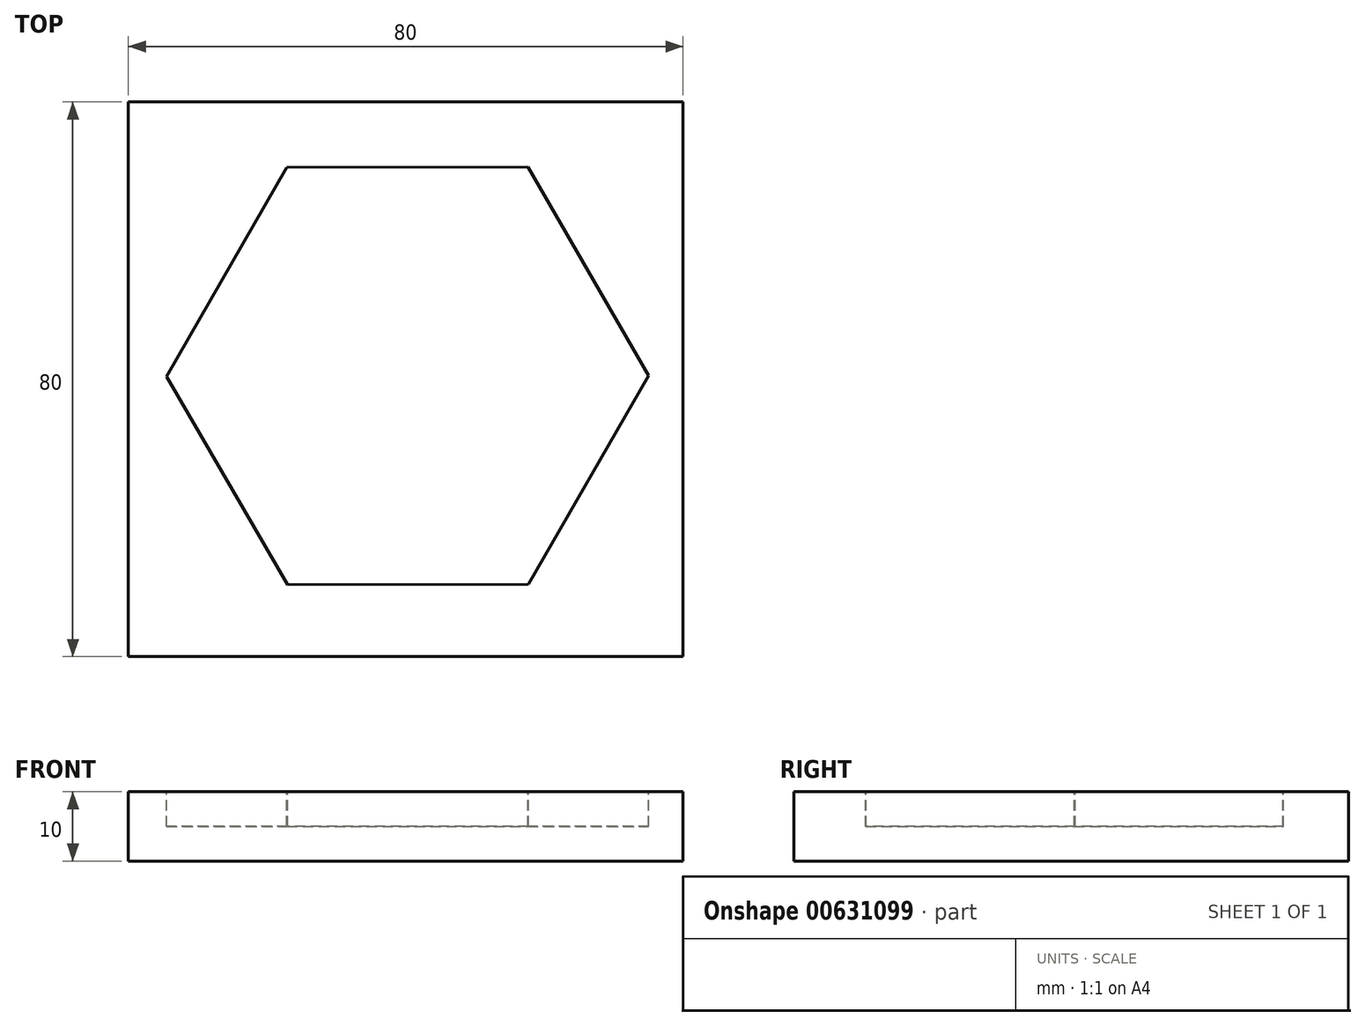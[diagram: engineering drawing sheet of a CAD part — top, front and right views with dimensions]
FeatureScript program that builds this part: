
annotation { "Feature Type Name" : "Feature", "Feature Type Description" : "" }
export const myFeature = defineFeature(function(context is Context, id is Id, definition is map)
    precondition{}
    {
        {
            var Q0;
            Q0=qCreatedBy(makeId("Top.planeOp"),FACE);
            var sketch = newSketch(context, id + "F0", { "sketchPlane" : qUnion([Q0])});
            skLineSegment(sketch, "E0.bottom", {"start": v(-45.18, 50.62) * mm, "end": v(34.82, 50.62) * mm});
            skLineSegment(sketch, "E0.top", {"start": v(-45.18, -29.38) * mm, "end": v(34.82, -29.38) * mm});
            skLineSegment(sketch, "E0.left", {"start": v(-45.18, 50.62) * mm, "end": v(-45.18, -29.38) * mm});
            skLineSegment(sketch, "E0.right", {"start": v(34.82, 50.62) * mm, "end": v(34.82, -29.38) * mm});
            skSolve(sketch);
        }
        {
            var Q0;
            Q0 = qSketchRegion(id + "F0", true);
            extrude(context, id + "F1", {"entities" : qUnion([Q0]), "depth" : 10 * mm, "offsetDistance" : 25 * mm});
        }
        {
            var Q0;
            Q0=makeQuery(id+"F1.opExtrude","CAP_FACE",FACE,{"disambiguationData":[OSD([sQuery(id+"F0.wireOp",EDGE,"E0.bottom"),sQuery(id+"F0.wireOp",EDGE,"E0.top"),sQuery(id+"F0.wireOp",EDGE,"E0.left"),sQuery(id+"F0.wireOp",EDGE,"E0.right")])],"isStart":false});
            var sketch = newSketch(context, id + "F2", { "sketchPlane" : qUnion([Q0])});
            skCircle(sketch, "E1.cCircle", {"center": v(-4.88, 11.1) * mm, "radius": 30.11 * mm, "construction": true});
            skLineSegment(sketch, "E1.0", {"start": v(-22.22, -19.04) * mm, "end": v(-39.65, 11.04) * mm});
            skLineSegment(sketch, "E1.1", {"start": v(-39.65, 11.04) * mm, "end": v(-22.32, 41.18) * mm});
            skLineSegment(sketch, "E1.2", {"start": v(-22.32, 41.18) * mm, "end": v(12.45, 41.24) * mm});
            skLineSegment(sketch, "E1.3", {"start": v(12.45, 41.24) * mm, "end": v(29.88, 11.16) * mm});
            skLineSegment(sketch, "E1.4", {"start": v(29.88, 11.16) * mm, "end": v(12.55, -18.98) * mm});
            skLineSegment(sketch, "E1.5", {"start": v(12.55, -18.98) * mm, "end": v(-22.22, -19.04) * mm});
            skPoint(sketch, "E1.0.midPoint", {"position": v(-30.94, -4) * mm});
            skSolve(sketch);
        }
        {
            var Q0;
            Q0=makeQuery(id+"F2.imprint","IMPRINT",FACE,{"disambiguationData":[TD([[makeQuery(id+"F2.imprint","IMPRINT",EDGE,{"derivedFrom":sQuery(id+"F2.wireOp",EDGE,"E1.0")}),-1.0]])]});
            extrude(context, id + "F3", {"entities" : qUnion([Q0]), "operationType" : NewBodyOperationType.REMOVE, "oppositeDirection" : true, "depth" : 5 * mm, "offsetDistance" : 25 * mm});
        }
    });
